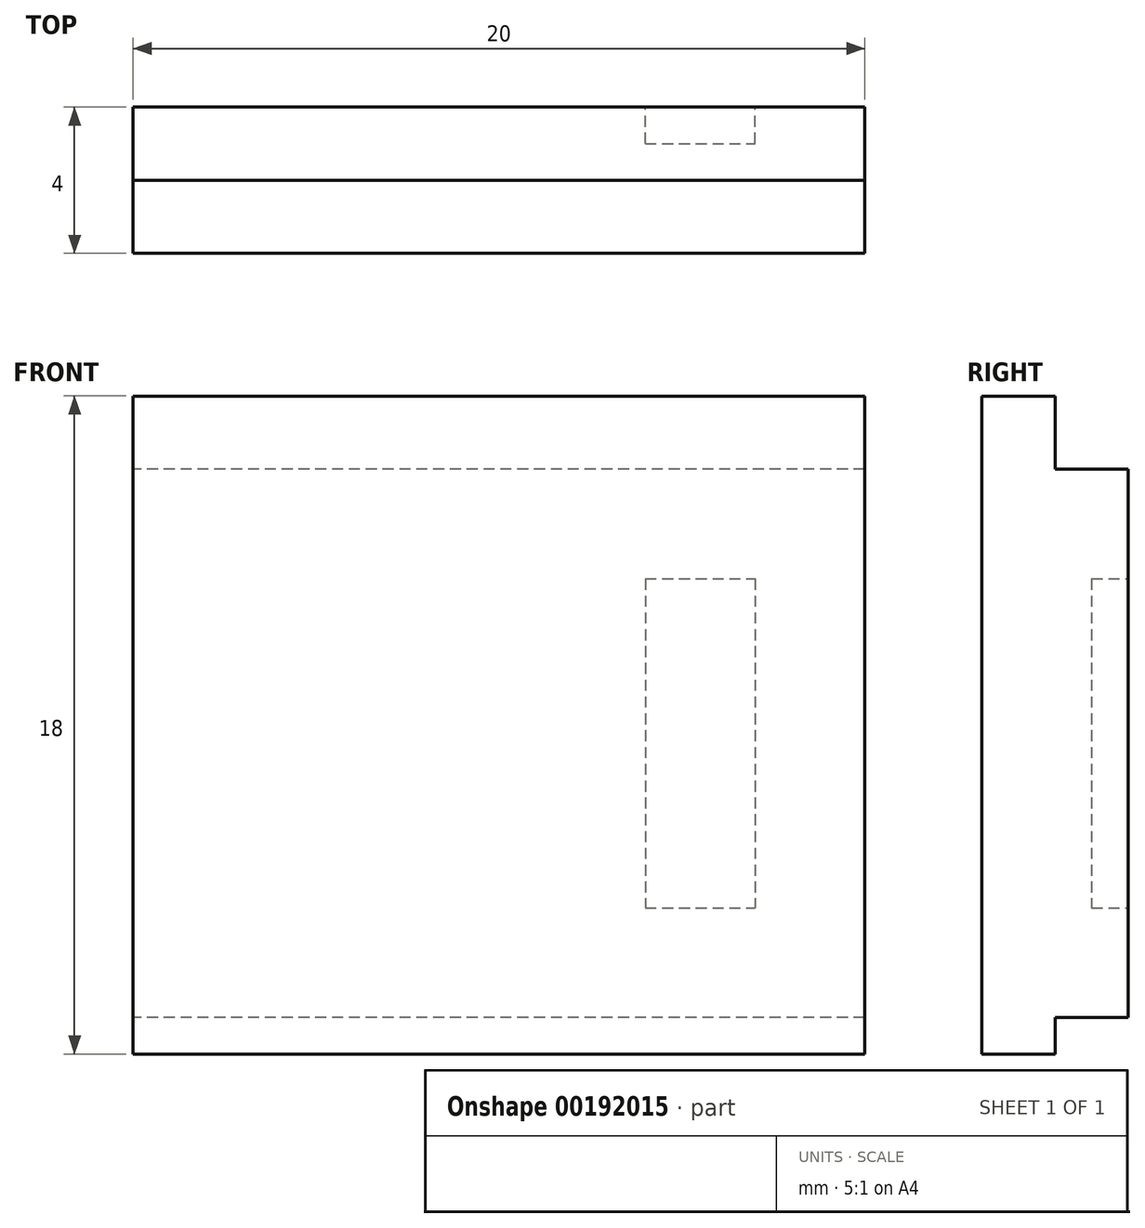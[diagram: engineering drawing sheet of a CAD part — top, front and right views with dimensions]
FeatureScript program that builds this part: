
annotation { "Feature Type Name" : "Feature", "Feature Type Description" : "" }
export const myFeature = defineFeature(function(context is Context, id is Id, definition is map)
    precondition{}
    {
        {
            var Q0;
            Q0=qCreatedBy(makeId("Right.planeOp"),FACE);
            var sketch = newSketch(context, id + "F0", { "sketchPlane" : qUnion([Q0])});
            skLineSegment(sketch, "E0", {"start": v(-0.03, 8.92) * mm, "end": v(1.97, 8.92) * mm});
            skLineSegment(sketch, "E1", {"start": v(1.97, 8.92) * mm, "end": v(1.97, -9.08) * mm});
            skLineSegment(sketch, "E2", {"start": v(1.97, -9.08) * mm, "end": v(-0.03, -9.08) * mm});
            skLineSegment(sketch, "E3", {"start": v(-0.03, -9.08) * mm, "end": v(-0.03, -8.08) * mm});
            skLineSegment(sketch, "E4", {"start": v(-0.03, -8.08) * mm, "end": v(-0.03, 6.92) * mm});
            skLineSegment(sketch, "E5", {"start": v(-0.03, 6.92) * mm, "end": v(-0.03, 8.92) * mm});
            skLineSegment(sketch, "E6", {"start": v(-0.03, 6.92) * mm, "end": v(3.97, 6.92) * mm});
            skLineSegment(sketch, "E7", {"start": v(3.97, 6.92) * mm, "end": v(3.97, -8.08) * mm});
            skLineSegment(sketch, "E8", {"start": v(3.97, -8.08) * mm, "end": v(-0.03, -8.08) * mm});
            skSolve(sketch);
        }
        {
            var Q0;
            {var subQ0=sQuery(id+"F0.wireOp",EDGE,"E0");Q0=makeQuery(id+"F0.imprint","IMPRINT",FACE,{"disambiguationData":[TD([[makeQuery(id+"F0.imprint","IMPRINT",EDGE,{"derivedFrom":subQ0}),-1.0]])]});}
            var Q1;
            {var subQ5=sQuery(id+"F0.wireOp",EDGE,"E4");Q1=makeQuery(id+"F0.imprint","IMPRINT",FACE,{"disambiguationData":[TD([[makeQuery(id+"F0.imprint","IMPRINT",EDGE,{"derivedFrom":subQ5}),-1.0]])]});}
            var Q2;
            {var subQ5=sQuery(id+"F0.wireOp",EDGE,"E7");Q2=makeQuery(id+"F0.imprint","IMPRINT",FACE,{"disambiguationData":[TD([[makeQuery(id+"F0.imprint","IMPRINT",EDGE,{"derivedFrom":subQ5}),-1.0]])]});}
            var Q3;
            {var subQ0=sQuery(id+"F0.wireOp",EDGE,"E2");Q3=makeQuery(id+"F0.imprint","IMPRINT",FACE,{"disambiguationData":[TD([[makeQuery(id+"F0.imprint","IMPRINT",EDGE,{"derivedFrom":subQ0}),-1.0]])]});}
            var Q4;
            Q4=sQuery(id+"F0.wireOp",EDGE,"81464b04-5446-45e9-9981-f51c669869ff");
            var Q5;
            Q5=sQuery(id+"F0.wireOp",EDGE,"078fc9a2-733a-492f-93f7-99a92d6bb3d3");
            var Q6;
            Q6=sQuery(id+"F0.wireOp",EDGE,"3b0ed797-3094-4dec-a863-a79e0f89327e");
            var Q7;
            Q7=sQuery(id+"F0.wireOp",EDGE,"ad86acff-b7a4-4d91-83df-e0d3c35a1710");
            var Q8;
            Q8=sQuery(id+"F0.wireOp",EDGE,"ef0bf857-1eff-408b-ad2d-1f2f2768b999");
            var Q9;
            Q9=sQuery(id+"F0.wireOp",EDGE,"8cc9f5da-0972-4caa-aa70-4e3f990f8aac");
            var Q10;
            Q10=sQuery(id+"F0.wireOp",EDGE,"5ba35cd9-c117-4e99-9e51-d512c0b651a3");
            var Q11;
            Q11=sQuery(id+"F0.wireOp",EDGE,"86540538-0233-4e82-a227-b6b84ec95295");
            var Q12;
            Q12=sQuery(id+"F0.wireOp",EDGE,"f274efa9-3706-4490-a5f7-80f8098b9e4a");
            extrude(context, id + "F1", {"entities" : qUnion([Q0, Q1, Q2, Q3]), "surfaceEntities" : qUnion([Q4, Q5, Q6, Q7, Q8, Q9, Q10, Q11, Q12]), "depth" : 20 * mm});
        }
        {
            var Q0;
            Q0=makeQuery(id+"F1.opExtrude","SWEPT_FACE",FACE,{"disambiguationData":[OSD([sQuery(id+"F0.wireOp",EDGE,"E7")])]});
            var sketch = newSketch(context, id + "F2", { "sketchPlane" : qUnion([Q0])});
            skLineSegment(sketch, "E9.bottom", {"start": v(-14, 3.92) * mm, "end": v(-17, 3.92) * mm});
            skLineSegment(sketch, "E9.top", {"start": v(-14, -5.08) * mm, "end": v(-17, -5.08) * mm});
            skLineSegment(sketch, "E9.left", {"start": v(-14, 3.92) * mm, "end": v(-14, -5.08) * mm});
            skLineSegment(sketch, "E9.right", {"start": v(-17, 3.92) * mm, "end": v(-17, -5.08) * mm});
            skSolve(sketch);
        }
        {
            var Q0;
            Q0 = qSketchRegion(id + "F2", true);
            extrude(context, id + "F3", {"entities" : qUnion([Q0]), "operationType" : NewBodyOperationType.REMOVE, "oppositeDirection" : true, "depth" : 1 * mm});
        }
    });
